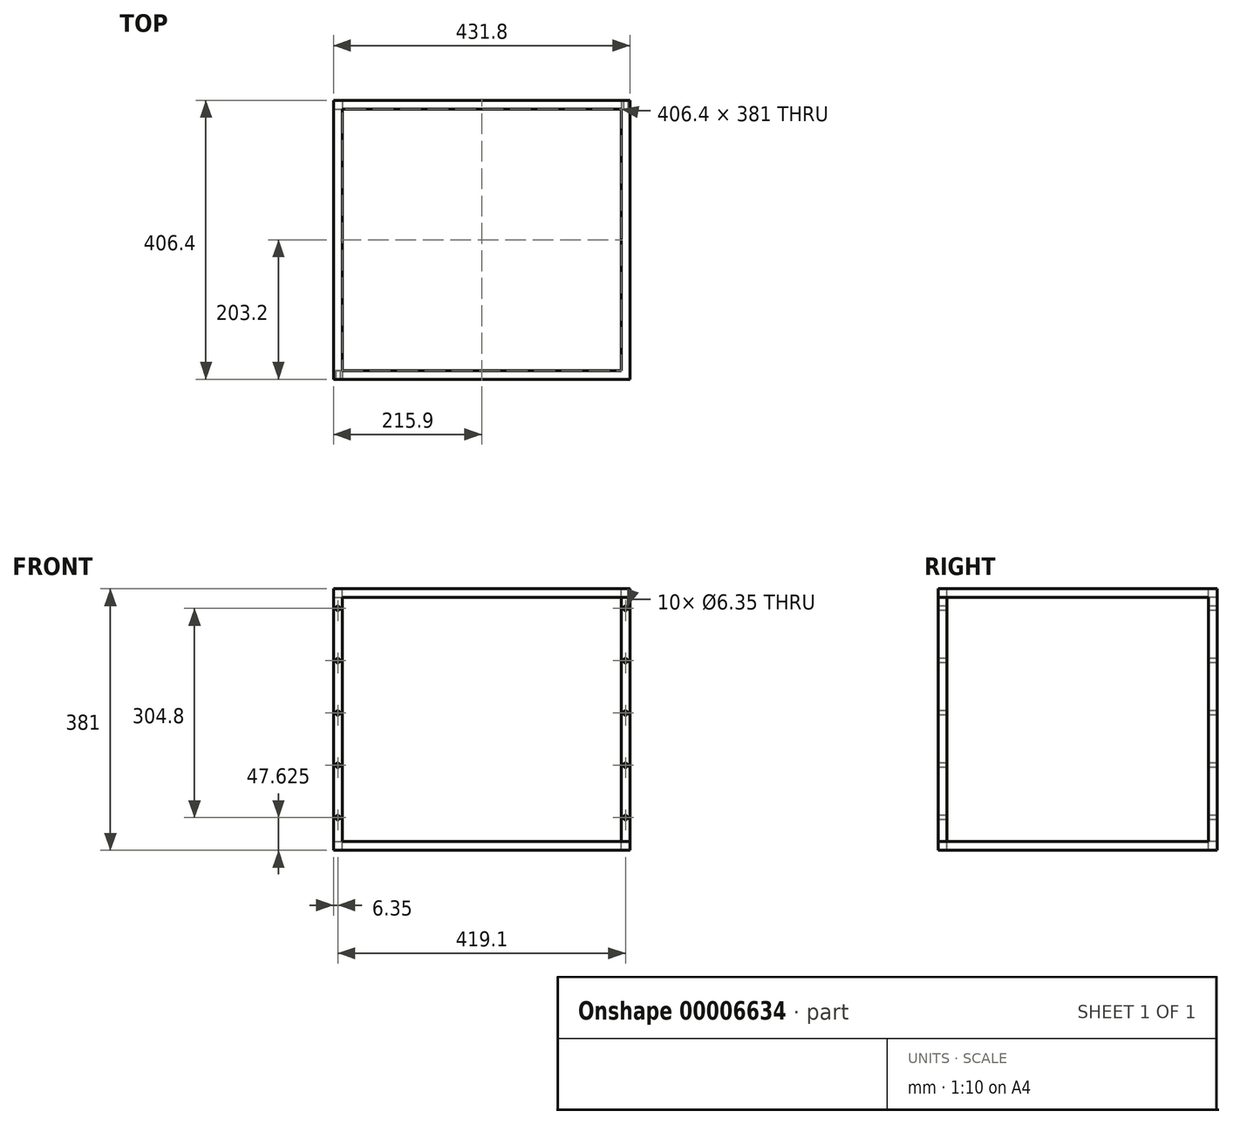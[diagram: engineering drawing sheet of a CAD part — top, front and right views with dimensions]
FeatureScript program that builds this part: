
annotation { "Feature Type Name" : "Feature", "Feature Type Description" : "" }
export const myFeature = defineFeature(function(context is Context, id is Id, definition is map)
    precondition{}
    {
        {
            var Q0;
            Q0=qCreatedBy(makeId("Front.planeOp"),FACE);
            var sketch = newSketch(context, id + "F0", { "sketchPlane" : qUnion([Q0])});
            skLineSegment(sketch, "E0.rect.bottom", {"start": v(215.9, 190.5) * mm, "end": v(-215.9, 190.5) * mm});
            skLineSegment(sketch, "E0.rect.top", {"start": v(215.9, -190.5) * mm, "end": v(-215.9, -190.5) * mm});
            skLineSegment(sketch, "E0.rect.left", {"start": v(215.9, 190.5) * mm, "end": v(215.9, -190.5) * mm});
            skLineSegment(sketch, "E0.rect.right", {"start": v(-215.9, 190.5) * mm, "end": v(-215.9, -190.5) * mm});
            skPoint(sketch, "E0.rect.middle", {"position": v(0, 0) * mm});
            skLineSegment(sketch, "E1", {"start": v(203.2, 190.5) * mm, "end": v(203.2, 177.8) * mm});
            skLineSegment(sketch, "E2", {"start": v(215.9, 177.8) * mm, "end": v(203.2, 177.8) * mm});
            skLineSegment(sketch, "E3", {"start": v(0, 202.13) * mm, "end": v(0, -199.96) * mm, "construction": true});
            skLineSegment(sketch, "E4", {"start": v(-280.54, 0) * mm, "end": v(237.67, 0) * mm, "construction": true});
            skLineSegment(sketch, "E5.0.MirrorCS", {"start": v(-203.2, 190.5) * mm, "end": v(-203.2, 177.8) * mm});
            skLineSegment(sketch, "E6.0.MirrorCS", {"start": v(-215.9, 177.8) * mm, "end": v(-203.2, 177.8) * mm});
            skLineSegment(sketch, "E7.0.MirrorCS", {"start": v(-203.2, -190.5) * mm, "end": v(-203.2, -177.8) * mm});
            skLineSegment(sketch, "E8.0.MirrorCS", {"start": v(-215.9, -177.8) * mm, "end": v(-203.2, -177.8) * mm});
            skLineSegment(sketch, "E9.0.MirrorCS", {"start": v(203.2, -190.5) * mm, "end": v(203.2, -177.8) * mm});
            skLineSegment(sketch, "E10.0.MirrorCS", {"start": v(215.9, -177.8) * mm, "end": v(203.2, -177.8) * mm});
            skLineSegment(sketch, "E11", {"start": v(-203.2, 177.8) * mm, "end": v(203.2, 177.8) * mm});
            skLineSegment(sketch, "E12", {"start": v(203.2, 177.8) * mm, "end": v(203.2, -177.8) * mm});
            skLineSegment(sketch, "E13", {"start": v(203.2, -177.8) * mm, "end": v(-203.2, -177.8) * mm});
            skLineSegment(sketch, "E14", {"start": v(-203.2, -177.8) * mm, "end": v(-203.2, 177.8) * mm});
            skLineSegment(sketch, "E15", {"start": v(-209.55, 206.37) * mm, "end": v(-209.55, -216.36) * mm, "construction": true});
            skCircle(sketch, "E16", {"center": v(-209.55, -142.87) * mm, "radius": 3.18 * mm});
            skCircle(sketch, "E17.0.1.0", {"center": v(-209.55, -66.67) * mm, "radius": 3.18 * mm});
            skLineSegment(sketch, "E17.0.1.1", {"start": v(203.2, -101.6) * mm, "end": v(-203.2, -101.6) * mm});
            skCircle(sketch, "E17.0.2.0", {"center": v(-209.55, 9.53) * mm, "radius": 3.18 * mm});
            skLineSegment(sketch, "E17.0.2.1", {"start": v(203.2, -25.4) * mm, "end": v(-203.2, -25.4) * mm});
            skCircle(sketch, "E17.0.3.0", {"center": v(-209.55, 85.73) * mm, "radius": 3.18 * mm});
            skLineSegment(sketch, "E17.0.3.1", {"start": v(203.2, 50.8) * mm, "end": v(-203.2, 50.8) * mm});
            skCircle(sketch, "E17.0.4.0", {"center": v(-209.55, 161.93) * mm, "radius": 3.18 * mm});
            skLineSegment(sketch, "E17.0.4.1", {"start": v(203.2, 127) * mm, "end": v(-203.2, 127) * mm});
            skLineSegment(sketch, "E17.direction1", {"start": v(-209.55, -142.87) * mm, "end": v(-184.15, -142.87) * mm, "construction": true});
            skLineSegment(sketch, "E17.direction2", {"start": v(-209.55, -142.87) * mm, "end": v(-209.55, -66.67) * mm, "construction": true});
            skCircle(sketch, "E18.0.MirrorC", {"center": v(209.55, 161.93) * mm, "radius": 3.18 * mm});
            skCircle(sketch, "E19.0.MirrorC", {"center": v(209.55, 85.73) * mm, "radius": 3.18 * mm});
            skCircle(sketch, "E20.0.MirrorC", {"center": v(209.55, 9.53) * mm, "radius": 3.18 * mm});
            skCircle(sketch, "E21.0.MirrorC", {"center": v(209.55, -66.67) * mm, "radius": 3.18 * mm});
            skCircle(sketch, "E22.0.MirrorC", {"center": v(209.55, -142.87) * mm, "radius": 3.18 * mm});
            skSolve(sketch);
        }
        {
            var Q0;
            {var subQ1=sQuery(id+"F0.wireOp",EDGE,"E5.0.MirrorCS");Q0=makeQuery(id+"F0.imprint","IMPRINT",FACE,{"disambiguationData":[TD([[makeQuery(id+"F0.imprint","IMPRINT",EDGE,{"derivedFrom":subQ1}),-1.0]])]});}
            var Q1;
            {var subQ1=sQuery(id+"F0.wireOp",EDGE,"E1");Q1=makeQuery(id+"F0.imprint","IMPRINT",FACE,{"disambiguationData":[TD([[makeQuery(id+"F0.imprint","IMPRINT",EDGE,{"derivedFrom":subQ1}),-1.0]])]});}
            var Q2;
            {var subQ0=sQuery(id+"F0.wireOp",EDGE,"E6.0.MirrorCS");Q2=makeQuery(id+"F0.imprint","IMPRINT",FACE,{"disambiguationData":[TD([[makeQuery(id+"F0.imprint","IMPRINT",EDGE,{"derivedFrom":subQ0}),-1.0]])]});}
            var Q3;
            {var subQ1=sQuery(id+"F0.wireOp",EDGE,"E7.0.MirrorCS");Q3=makeQuery(id+"F0.imprint","IMPRINT",FACE,{"disambiguationData":[TD([[makeQuery(id+"F0.imprint","IMPRINT",EDGE,{"derivedFrom":subQ1}),1.0]])]});}
            var Q4;
            {var subQ1=sQuery(id+"F0.wireOp",EDGE,"E7.0.MirrorCS");Q4=makeQuery(id+"F0.imprint","IMPRINT",FACE,{"disambiguationData":[TD([[makeQuery(id+"F0.imprint","IMPRINT",EDGE,{"derivedFrom":subQ1}),-1.0]])]});}
            var Q5;
            {var subQ1=sQuery(id+"F0.wireOp",EDGE,"E1");Q5=makeQuery(id+"F0.imprint","IMPRINT",FACE,{"disambiguationData":[TD([[makeQuery(id+"F0.imprint","IMPRINT",EDGE,{"derivedFrom":subQ1}),1.0]])]});}
            var Q6;
            {var subQ1=sQuery(id+"F0.wireOp",EDGE,"E2");Q6=makeQuery(id+"F0.imprint","IMPRINT",FACE,{"disambiguationData":[TD([[makeQuery(id+"F0.imprint","IMPRINT",EDGE,{"derivedFrom":subQ1}),1.0]])]});}
            var Q7;
            {var subQ0=sQuery(id+"F0.wireOp",EDGE,"E9.0.MirrorCS");Q7=makeQuery(id+"F0.imprint","IMPRINT",FACE,{"disambiguationData":[TD([[makeQuery(id+"F0.imprint","IMPRINT",EDGE,{"derivedFrom":subQ0}),-1.0]])]});}
            var Q8;
            Q8=makeQuery(id+"F0.imprint","IMPRINT",FACE,{"disambiguationData":[TD([[makeQuery(id+"F0.imprint","IMPRINT",EDGE,{"derivedFrom":sQuery(id+"F0.wireOp",EDGE,"E17.0.4.0")}),1.0]])]});
            var Q9;
            Q9=makeQuery(id+"F0.imprint","IMPRINT",FACE,{"disambiguationData":[TD([[makeQuery(id+"F0.imprint","IMPRINT",EDGE,{"derivedFrom":sQuery(id+"F0.wireOp",EDGE,"E17.0.3.0")}),1.0]])]});
            var Q10;
            Q10=makeQuery(id+"F0.imprint","IMPRINT",FACE,{"disambiguationData":[TD([[makeQuery(id+"F0.imprint","IMPRINT",EDGE,{"derivedFrom":sQuery(id+"F0.wireOp",EDGE,"E17.0.2.0")}),1.0]])]});
            var Q11;
            Q11=makeQuery(id+"F0.imprint","IMPRINT",FACE,{"disambiguationData":[TD([[makeQuery(id+"F0.imprint","IMPRINT",EDGE,{"derivedFrom":sQuery(id+"F0.wireOp",EDGE,"E16")}),1.0]])]});
            var Q12;
            Q12=makeQuery(id+"F0.imprint","IMPRINT",FACE,{"disambiguationData":[TD([[makeQuery(id+"F0.imprint","IMPRINT",EDGE,{"derivedFrom":sQuery(id+"F0.wireOp",EDGE,"E17.0.1.0")}),1.0]])]});
            var Q13;
            Q13=makeQuery(id+"F0.imprint","IMPRINT",FACE,{"disambiguationData":[TD([[makeQuery(id+"F0.imprint","IMPRINT",EDGE,{"derivedFrom":sQuery(id+"F0.wireOp",EDGE,"E18.0.MirrorC")}),-1.0]])]});
            var Q14;
            Q14=makeQuery(id+"F0.imprint","IMPRINT",FACE,{"disambiguationData":[TD([[makeQuery(id+"F0.imprint","IMPRINT",EDGE,{"derivedFrom":sQuery(id+"F0.wireOp",EDGE,"E19.0.MirrorC")}),-1.0]])]});
            var Q15;
            Q15=makeQuery(id+"F0.imprint","IMPRINT",FACE,{"disambiguationData":[TD([[makeQuery(id+"F0.imprint","IMPRINT",EDGE,{"derivedFrom":sQuery(id+"F0.wireOp",EDGE,"E20.0.MirrorC")}),-1.0]])]});
            var Q16;
            Q16=makeQuery(id+"F0.imprint","IMPRINT",FACE,{"disambiguationData":[TD([[makeQuery(id+"F0.imprint","IMPRINT",EDGE,{"derivedFrom":sQuery(id+"F0.wireOp",EDGE,"E21.0.MirrorC")}),-1.0]])]});
            var Q17;
            Q17=makeQuery(id+"F0.imprint","IMPRINT",FACE,{"disambiguationData":[TD([[makeQuery(id+"F0.imprint","IMPRINT",EDGE,{"derivedFrom":sQuery(id+"F0.wireOp",EDGE,"E22.0.MirrorC")}),-1.0]])]});
            extrude(context, id + "F1", {"entities" : qUnion([Q0, Q1, Q2, Q3, Q4, Q5, Q6, Q7, Q8, Q9, Q10, Q11, Q12, Q13, Q14, Q15, Q16, Q17]), "oppositeDirection" : true, "depth" : 406.4 * mm});
        }
        {
            var Q0;
            Q0=makeQuery(id+"F1.opExtrude","SWEPT_FACE",FACE,{"disambiguationData":[OSD([sQuery(id+"F0.wireOp",EDGE,"E0.rect.bottom")])]});
            var sketch = newSketch(context, id + "F2", { "sketchPlane" : qUnion([Q0])});
            skLineSegment(sketch, "E23", {"start": v(-215.9, 406.4) * mm, "end": v(215.9, 406.4) * mm});
            skLineSegment(sketch, "E24", {"start": v(-215.9, 0) * mm, "end": v(215.9, 0) * mm});
            skLineSegment(sketch, "E25", {"start": v(215.9, 0) * mm, "end": v(215.9, 406.4) * mm});
            skLineSegment(sketch, "E26", {"start": v(-215.9, 406.4) * mm, "end": v(-215.9, 0) * mm});
            skLineSegment(sketch, "E27.0", {"start": v(-215.9, 393.7) * mm, "end": v(215.9, 393.7) * mm});
            skLineSegment(sketch, "E28.0", {"start": v(-203.2, 406.4) * mm, "end": v(-203.2, 0) * mm});
            skLineSegment(sketch, "E29.0", {"start": v(203.2, 0) * mm, "end": v(203.2, 406.4) * mm});
            skLineSegment(sketch, "E30.0", {"start": v(-215.9, 12.7) * mm, "end": v(215.9, 12.7) * mm});
            skSolve(sketch);
        }
        {
            var Q0;
            {var subQ3=sQuery(id+"F2.wireOp",EDGE,"E28.0");var subQ5=sQuery(id+"F2.wireOp",EDGE,"E27.0");var subQ7=makeQuery(id+"F2.imprint","INTERSECT",VERTEX,{"derivedFrom":[subQ5,subQ3]});Q0=makeQuery(id+"F2.imprint","IMPRINT",FACE,{"disambiguationData":[TD([[makeQuery(id+"F2.imprint","IMPRINT",EDGE,{"disambiguationData":[TD([[subQ7,-1.0]])],"derivedFrom":subQ5}),-1.0]])]});}
            extrude(context, id + "F3", {"entities" : qUnion([Q0]), "operationType" : NewBodyOperationType.REMOVE, "oppositeDirection" : true, "depth" : 381 * mm});
        }
        {
            var Q0;
            Q0=makeQuery(id+"F1.opExtrude","SWEPT_FACE",FACE,{"disambiguationData":[OSD([sQuery(id+"F0.wireOp",EDGE,"E0.rect.left")])]});
            var sketch = newSketch(context, id + "F4", { "sketchPlane" : qUnion([Q0])});
            skLineSegment(sketch, "E31", {"start": v(0, 190.5) * mm, "end": v(406.4, 190.5) * mm});
            skLineSegment(sketch, "E32", {"start": v(406.4, 190.5) * mm, "end": v(406.4, -190.5) * mm});
            skLineSegment(sketch, "E33", {"start": v(406.4, -190.5) * mm, "end": v(0, -190.5) * mm});
            skLineSegment(sketch, "E34", {"start": v(0, -190.5) * mm, "end": v(0, 190.5) * mm});
            skLineSegment(sketch, "E35.0", {"start": v(12.7, 177.8) * mm, "end": v(393.7, 177.8) * mm});
            skLineSegment(sketch, "E35.1", {"start": v(12.7, -177.8) * mm, "end": v(12.7, 177.8) * mm});
            skLineSegment(sketch, "E35.2", {"start": v(393.7, -177.8) * mm, "end": v(12.7, -177.8) * mm});
            skLineSegment(sketch, "E35.3", {"start": v(393.7, 177.8) * mm, "end": v(393.7, -177.8) * mm});
            skSolve(sketch);
        }
        {
            var Q0;
            Q0=makeQuery(id+"F4.imprint","IMPRINT",FACE,{"disambiguationData":[TD([[makeQuery(id+"F4.imprint","IMPRINT",EDGE,{"derivedFrom":sQuery(id+"F4.wireOp",EDGE,"E35.0")}),-1.0]])]});
            extrude(context, id + "F5", {"entities" : qUnion([Q0]), "operationType" : NewBodyOperationType.REMOVE, "oppositeDirection" : true, "depth" : 431.8 * mm});
        }
        {
            var Q0;
            Q0=makeQuery(id+"F0.imprint","IMPRINT",FACE,{"disambiguationData":[TD([[makeQuery(id+"F0.imprint","IMPRINT",EDGE,{"derivedFrom":sQuery(id+"F0.wireOp",EDGE,"E16")}),1.0]])]});
            var Q1;
            Q1=makeQuery(id+"F0.imprint","IMPRINT",FACE,{"disambiguationData":[TD([[makeQuery(id+"F0.imprint","IMPRINT",EDGE,{"derivedFrom":sQuery(id+"F0.wireOp",EDGE,"E17.0.1.0")}),1.0]])]});
            var Q2;
            Q2=makeQuery(id+"F0.imprint","IMPRINT",FACE,{"disambiguationData":[TD([[makeQuery(id+"F0.imprint","IMPRINT",EDGE,{"derivedFrom":sQuery(id+"F0.wireOp",EDGE,"E17.0.2.0")}),1.0]])]});
            var Q3;
            Q3=makeQuery(id+"F0.imprint","IMPRINT",FACE,{"disambiguationData":[TD([[makeQuery(id+"F0.imprint","IMPRINT",EDGE,{"derivedFrom":sQuery(id+"F0.wireOp",EDGE,"E17.0.3.0")}),1.0]])]});
            var Q4;
            Q4=makeQuery(id+"F0.imprint","IMPRINT",FACE,{"disambiguationData":[TD([[makeQuery(id+"F0.imprint","IMPRINT",EDGE,{"derivedFrom":sQuery(id+"F0.wireOp",EDGE,"E17.0.4.0")}),1.0]])]});
            var Q5;
            Q5=makeQuery(id+"F0.imprint","IMPRINT",FACE,{"disambiguationData":[TD([[makeQuery(id+"F0.imprint","IMPRINT",EDGE,{"derivedFrom":sQuery(id+"F0.wireOp",EDGE,"E18.0.MirrorC")}),-1.0]])]});
            var Q6;
            Q6=makeQuery(id+"F0.imprint","IMPRINT",FACE,{"disambiguationData":[TD([[makeQuery(id+"F0.imprint","IMPRINT",EDGE,{"derivedFrom":sQuery(id+"F0.wireOp",EDGE,"E19.0.MirrorC")}),-1.0]])]});
            var Q7;
            Q7=makeQuery(id+"F0.imprint","IMPRINT",FACE,{"disambiguationData":[TD([[makeQuery(id+"F0.imprint","IMPRINT",EDGE,{"derivedFrom":sQuery(id+"F0.wireOp",EDGE,"E20.0.MirrorC")}),-1.0]])]});
            var Q8;
            Q8=makeQuery(id+"F0.imprint","IMPRINT",FACE,{"disambiguationData":[TD([[makeQuery(id+"F0.imprint","IMPRINT",EDGE,{"derivedFrom":sQuery(id+"F0.wireOp",EDGE,"E21.0.MirrorC")}),-1.0]])]});
            var Q9;
            Q9=makeQuery(id+"F0.imprint","IMPRINT",FACE,{"disambiguationData":[TD([[makeQuery(id+"F0.imprint","IMPRINT",EDGE,{"derivedFrom":sQuery(id+"F0.wireOp",EDGE,"E22.0.MirrorC")}),-1.0]])]});
            extrude(context, id + "F6", {"entities" : qUnion([Q0, Q1, Q2, Q3, Q4, Q5, Q6, Q7, Q8, Q9]), "operationType" : NewBodyOperationType.REMOVE, "oppositeDirection" : true, "depth" : 12.7 * mm});
        }
    });
